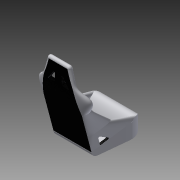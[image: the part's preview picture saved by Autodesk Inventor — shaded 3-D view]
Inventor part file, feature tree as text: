
AUTODESK INVENTOR PART (.ipt)
format: ipt  version: 2016 (Build 200138000, 138)  size: 1,221,120 bytes
history: native  units: in
note: dims shown in document units (in); Inventor stores cm internally (conversion verified against a paired STEP export)
features: other x2, imported_body x2, revolve x1
ambient origin geometry x8: Origin, YZ Plane, XZ Plane, XY Plane, X Axis, Y Axis, Z Axis, Center Point
bodies: Body1 (feature_tree), Body2 (feature_tree)
feature tree (5):
  revolve  "Revolve7"  [1 undecoded]
  other  "siege1"
  other  "Cut-Extrude11"
  imported_body  "Base1"
  imported_body  "Base2"
note: 1 required parameter value undecoded (feature->parameter linkage not recoverable at this tier; creation-order binding heuristic only, values carry confidence <= 0.55)
